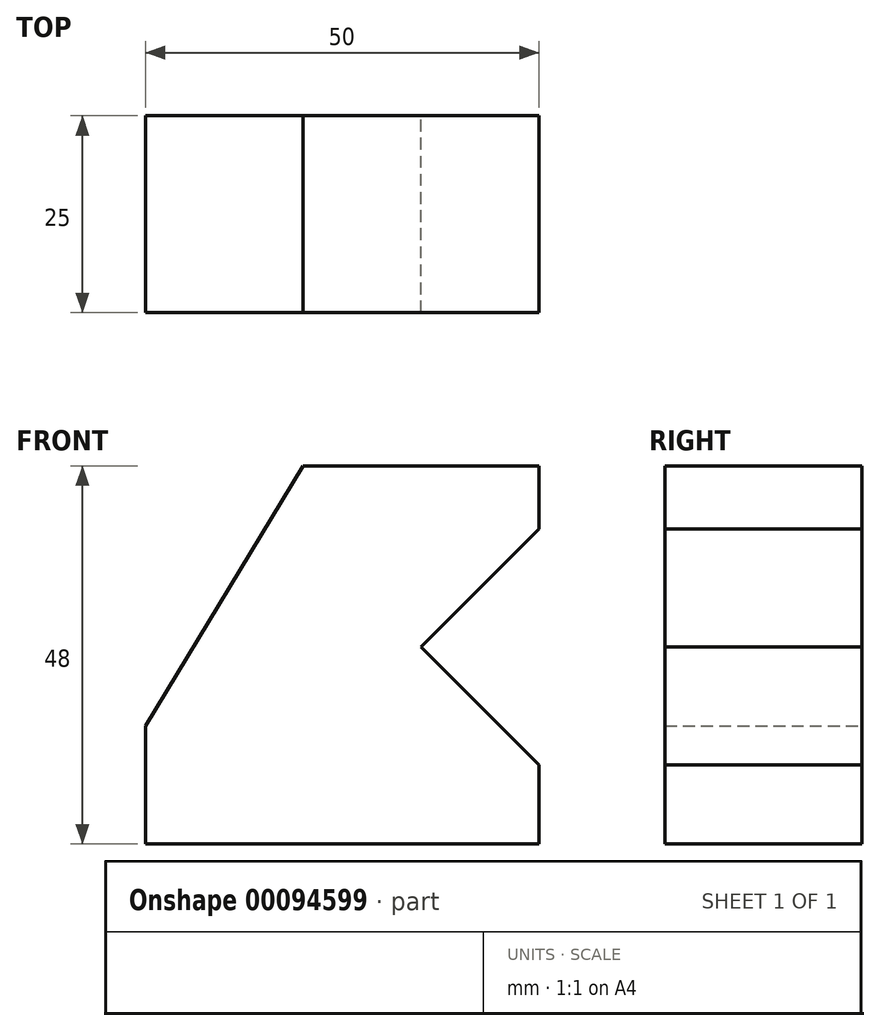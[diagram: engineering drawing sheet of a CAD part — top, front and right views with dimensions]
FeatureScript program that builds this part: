
annotation { "Feature Type Name" : "Feature", "Feature Type Description" : "" }
export const myFeature = defineFeature(function(context is Context, id is Id, definition is map)
    precondition{}
    {
        {
            var Q0;
            Q0=qCreatedBy(makeId("Front.planeOp"),FACE);
            var sketch = newSketch(context, id + "F0", { "sketchPlane" : qUnion([Q0])});
            skLineSegment(sketch, "E0", {"start": v(0, 0) * mm, "end": v(50, 0) * mm});
            skLineSegment(sketch, "E1", {"start": v(50, 48) * mm, "end": v(20, 48) * mm});
            skLineSegment(sketch, "E2", {"start": v(0, 0) * mm, "end": v(0, 15) * mm});
            skLineSegment(sketch, "E3", {"start": v(0, 15) * mm, "end": v(20, 48) * mm});
            skLineSegment(sketch, "E4", {"start": v(50, 0) * mm, "end": v(50, 10) * mm});
            skLineSegment(sketch, "E5", {"start": v(50, 0) * mm, "end": v(35, 0) * mm});
            skLineSegment(sketch, "E6", {"start": v(50, 48) * mm, "end": v(50, 40) * mm});
            skLineSegment(sketch, "E7", {"start": v(35, 25) * mm, "end": v(50, 40) * mm});
            skLineSegment(sketch, "E8", {"start": v(35, 25) * mm, "end": v(50, 10) * mm});
            skSolve(sketch);
        }
        {
            var Q0;
            Q0=makeQuery(id+"F0.imprint","IMPRINT",FACE,{"disambiguationData":[TD([[makeQuery(id+"F0.imprint","IMPRINT",EDGE,{"derivedFrom":sQuery(id+"F0.wireOp",EDGE,"E0")}),1.0]])]});
            extrude(context, id + "F1", {"entities" : qUnion([Q0]), "depth" : 25 * mm});
        }
    });
